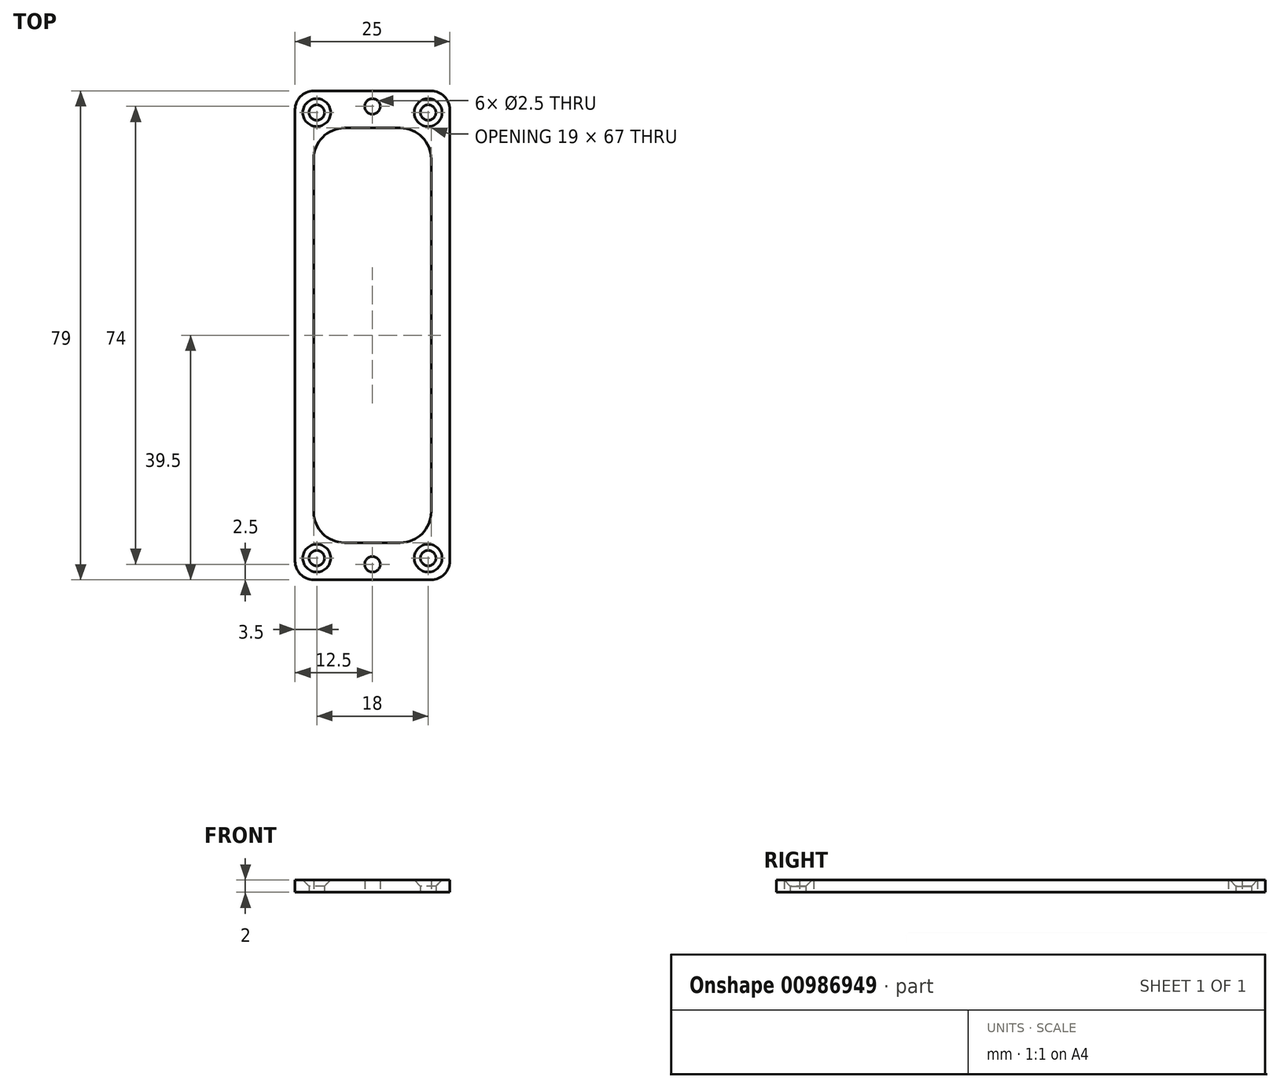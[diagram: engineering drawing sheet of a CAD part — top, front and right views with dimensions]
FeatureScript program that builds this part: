
annotation { "Feature Type Name" : "Feature", "Feature Type Description" : "" }
export const myFeature = defineFeature(function(context is Context, id is Id, definition is map)
    precondition{}
    {
        {
            var Q0;
            Q0=qCreatedBy(makeId("Top.planeOp"),FACE);
            var sketch = newSketch(context, id + "F0", { "sketchPlane" : qUnion([Q0])});
            skLineSegment(sketch, "E0.bottom", {"start": v(-4.5, 33.5) * mm, "end": v(4.5, 33.5) * mm});
            skLineSegment(sketch, "E0.top", {"start": v(-4.5, -33.5) * mm, "end": v(4.5, -33.5) * mm});
            skLineSegment(sketch, "E0.left", {"start": v(-9.5, 28.5) * mm, "end": v(-9.5, -28.5) * mm});
            skLineSegment(sketch, "E0.right", {"start": v(9.5, 28.5) * mm, "end": v(9.5, -28.5) * mm});
            skPoint(sketch, "E0.middle", {"position": v(0, 0) * mm});
            skLineSegment(sketch, "E1.bottom", {"start": v(-9.5, 39.5) * mm, "end": v(9.5, 39.5) * mm});
            skLineSegment(sketch, "E1.top", {"start": v(-9.5, -39.5) * mm, "end": v(9.5, -39.5) * mm});
            skLineSegment(sketch, "E1.left", {"start": v(-12.5, 36.5) * mm, "end": v(-12.5, -36.5) * mm});
            skLineSegment(sketch, "E1.right", {"start": v(12.5, 36.5) * mm, "end": v(12.5, -36.5) * mm});
            skPoint(sketch, "E2.visualSharp", {"position": v(-9.5, 33.5) * mm});
            skArc(sketch, "E2.filletArc", {"start": v(-4.5, 33.5) * mm, "mid": v(-8.04, 32.04) * mm, "end": v(-9.5, 28.5) * mm});
            skPoint(sketch, "E3.visualSharp", {"position": v(9.5, 33.5) * mm});
            skArc(sketch, "E3.filletArc", {"start": v(9.5, 28.5) * mm, "mid": v(8.04, 32.04) * mm, "end": v(4.5, 33.5) * mm});
            skPoint(sketch, "E4.visualSharp", {"position": v(9.5, -33.5) * mm});
            skArc(sketch, "E4.filletArc", {"start": v(4.5, -33.5) * mm, "mid": v(8.04, -32.04) * mm, "end": v(9.5, -28.5) * mm});
            skPoint(sketch, "E5.visualSharp", {"position": v(-9.5, -33.5) * mm});
            skArc(sketch, "E5.filletArc", {"start": v(-9.5, -28.5) * mm, "mid": v(-8.04, -32.04) * mm, "end": v(-4.5, -33.5) * mm});
            skPoint(sketch, "E6.visualSharp", {"position": v(-12.5, -39.5) * mm});
            skArc(sketch, "E6.filletArc", {"start": v(-12.5, -36.5) * mm, "mid": v(-11.62, -38.62) * mm, "end": v(-9.5, -39.5) * mm});
            skPoint(sketch, "E7.visualSharp", {"position": v(-12.5, 39.5) * mm});
            skArc(sketch, "E7.filletArc", {"start": v(-9.5, 39.5) * mm, "mid": v(-11.62, 38.62) * mm, "end": v(-12.5, 36.5) * mm});
            skPoint(sketch, "E8.visualSharp", {"position": v(12.5, 39.5) * mm});
            skArc(sketch, "E8.filletArc", {"start": v(12.5, 36.5) * mm, "mid": v(11.62, 38.62) * mm, "end": v(9.5, 39.5) * mm});
            skPoint(sketch, "E9.visualSharp", {"position": v(12.5, -39.5) * mm});
            skArc(sketch, "E9.filletArc", {"start": v(9.5, -39.5) * mm, "mid": v(11.62, -38.62) * mm, "end": v(12.5, -36.5) * mm});
            skCircle(sketch, "E10", {"center": v(0, -37) * mm, "radius": 1.25 * mm});
            skCircle(sketch, "E11", {"center": v(-9, -36) * mm, "radius": 1.25 * mm});
            skCircle(sketch, "E12", {"center": v(9, -36) * mm, "radius": 1.25 * mm});
            skCircle(sketch, "E13", {"center": v(-9, 36) * mm, "radius": 1.25 * mm});
            skCircle(sketch, "E14", {"center": v(0, 37) * mm, "radius": 1.25 * mm});
            skCircle(sketch, "E15", {"center": v(9, 36) * mm, "radius": 1.25 * mm});
            skSolve(sketch);
        }
        {
            var Q0;
            Q0 = qSketchRegion(id + "F0", true);
            extrude(context, id + "F1", {"entities" : qUnion([Q0]), "endBound" : BoundingType.SYMMETRIC, "depth" : 2 * mm, "offsetDistance" : 25 * mm});
        }
        {
            var Q0;
            Q0=makeQuery(id+"F1.opExtrude","CAP_EDGE",EDGE,{"disambiguationData":[OSD([sQuery(id+"F0.wireOp",EDGE,"E13")])],"isStart":false});
            var Q1;
            Q1=makeQuery(id+"F1.opExtrude","CAP_EDGE",EDGE,{"disambiguationData":[OSD([sQuery(id+"F0.wireOp",EDGE,"E15")])],"isStart":false});
            var Q2;
            Q2=makeQuery(id+"F1.opExtrude","CAP_EDGE",EDGE,{"disambiguationData":[OSD([sQuery(id+"F0.wireOp",EDGE,"E12")])],"isStart":false});
            var Q3;
            Q3=makeQuery(id+"F1.opExtrude","CAP_EDGE",EDGE,{"disambiguationData":[OSD([sQuery(id+"F0.wireOp",EDGE,"E11")])],"isStart":false});
            chamfer(context, id + "F2", {"entities" : qUnion([Q0, Q1, Q2, Q3]), "width" : 1 * mm, "tangentPropagation" : true});
        }
    });
